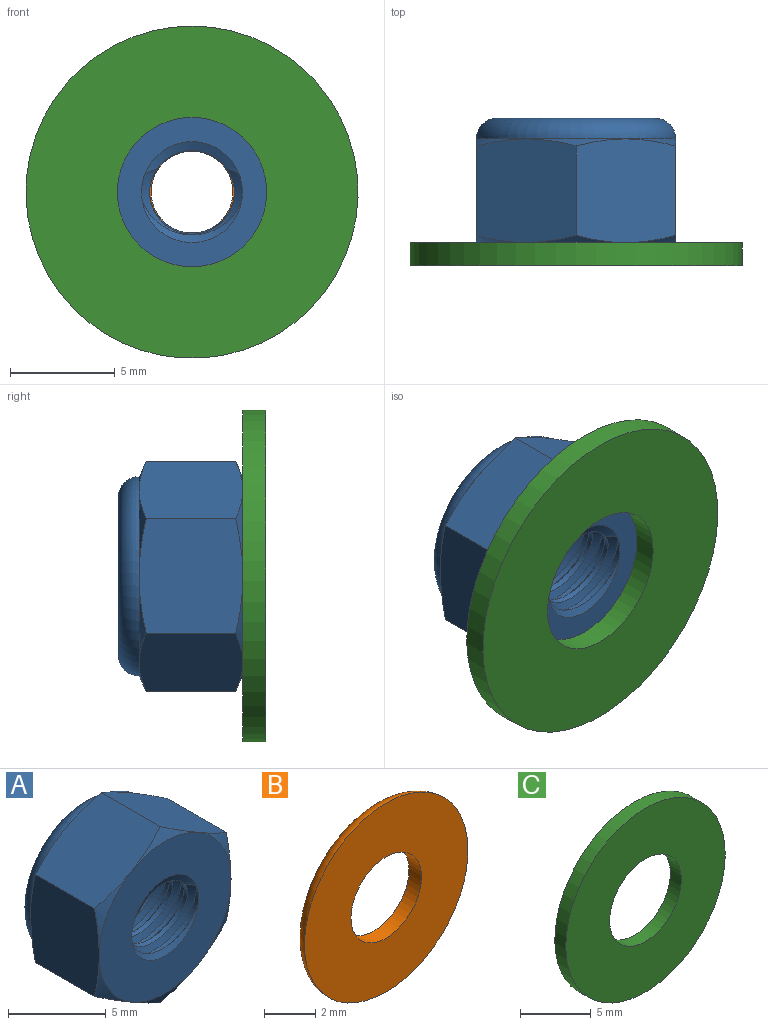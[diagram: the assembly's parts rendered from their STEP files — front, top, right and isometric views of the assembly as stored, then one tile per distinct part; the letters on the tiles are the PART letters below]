
ASSEMBLY  parts=3 mates=2
PART A: 50 faces, bbox 11.4x6.6x11.4 mm
  f0: torus R=3.77mm, axis (0,-1,0), area 35.7mm2, adj f48,f49
  f1: cylinder r=2.86mm len=5.72mm, axis (0,-1,0), area 2.7mm2, adj f26,f49
  f2: torus R=3.77mm, axis (0,-1,0), area 43.1mm2, adj f3,f26,f37,f38,f39,f40,f41
  f3: cone r=4.76mm half-angle=65deg, axis (0,-1,0), area 2.1mm2, adj f2,f46,f47
  f4: cone r=5.5mm half-angle=65deg, axis (0,1,0), area 2.1mm2, adj f27,f43,f44
  f5: cone r=2.6mm half-angle=60deg, axis (0,0.98,0.21), area 7.4mm2, adj f20,f23
  f6: cone r=2.03mm half-angle=60deg, axis (0,-0.98,-0.21), area 7.4mm2, adj f7,f20
  f7: cylinder r=2.03mm len=4.06mm, axis (0,0.98,0.21), area 3.4mm2, adj f6,f8
  f8: cone r=2.6mm half-angle=60deg, axis (0,0.98,0.21), area 7.4mm2, adj f7,f19
  f9: cone r=2.03mm half-angle=60deg, axis (0,-0.98,-0.21), area 7.4mm2, adj f10,f19
  f10: cylinder r=2.03mm len=4.06mm, axis (0,0.98,0.21), area 3.4mm2, adj f9,f11
  f11: cone r=2.6mm half-angle=60deg, axis (0,0.98,0.21), area 7.4mm2, adj f10,f18
  f12: cone r=2.03mm half-angle=60deg, axis (0,-0.98,-0.21), area 7.4mm2, adj f13,f18
  f13: cylinder r=2.03mm len=4.06mm, axis (0,0.98,0.21), area 3.4mm2, adj f12,f14
  f14: cone r=2.6mm half-angle=60deg, axis (0,0.98,0.21), area 7.4mm2, adj f13,f17
  f15: cylinder r=2.03mm len=4.06mm, axis (0,0.98,0.21), area 2.1mm2, adj f16,f31,f48
  f16: cone r=2.6mm half-angle=60deg, axis (0,0.98,0.21), area 2.6mm2, adj f15,f30,f48
  f17: cylinder r=2.41mm len=4.83mm, axis (0,-1,0), area 4.3mm2, adj f14,f31,f48
  f18: cylinder r=2.41mm len=4.83mm, axis (0,-1,0), area 4.4mm2, adj f11,f12
  f19: cylinder r=2.41mm len=4.83mm, axis (0,-1,0), area 4.4mm2, adj f8,f9
  f20: cylinder r=2.41mm len=4.83mm, axis (0,-1,0), area 4.4mm2, adj f5,f6
  f21: cylinder r=2.41mm len=4.83mm, axis (0,-1,0), area 1.9mm2, adj f22,f27,f29
  f22: cone r=2.03mm half-angle=60deg, axis (0,-0.98,-0.21), area 4.3mm2, adj f21,f23,f25
  f23: cylinder r=2.03mm len=4.06mm, axis (0,0.98,0.21), area 2.9mm2, adj f5,f22,f25
  f24: cone r=2.41mm half-angle=65deg, axis (0,-1,0), area 1.3mm2, adj f27,f29
  f25: cone r=2.41mm half-angle=65deg, axis (0,-1,0), area 2.2mm2, adj f22,f23,f27
  f26: plane 7.54x7.54mm, normal (0,1,0), area 18.9mm2, adj f1,f2
  f27: plane 9.53x9.53mm, normal (0,-1,0), area 53mm2, adj f4,f21,f24,f25,f32,f33,f34,f35
  f28: cone r=2.03mm half-angle=60deg, axis (0,-0.98,-0.21), area 0mm2, adj f30,f48
  f29: cone r=2.6mm half-angle=60deg, axis (0,0.98,0.21), area 1.6mm2, adj f21,f24
  f30: cylinder r=2.41mm len=4.45mm, axis (0,-1,0), area 0.9mm2, adj f16,f28,f48
  f31: cone r=2.03mm half-angle=60deg, axis (0,-0.98,-0.21), area 6.1mm2, adj f15,f17,f48
  f32: cone r=5.5mm half-angle=65deg, axis (0,1,0), area 2.1mm2, adj f27,f46,f47
  f33: cone r=5.5mm half-angle=65deg, axis (0,1,0), area 2.1mm2, adj f27,f42,f47
  f34: cone r=5.5mm half-angle=65deg, axis (0,1,0), area 2.1mm2, adj f27,f42,f43
  f35: cone r=5.5mm half-angle=65deg, axis (0,1,0), area 2.1mm2, adj f27,f44,f45
  f36: cone r=5.5mm half-angle=65deg, axis (0,1,0), area 2.1mm2, adj f27,f45,f46
  f37: cone r=4.76mm half-angle=65deg, axis (0,-1,0), area 2.1mm2, adj f2,f44,f45
  f38: cone r=4.76mm half-angle=65deg, axis (0,-1,0), area 2.1mm2, adj f2,f45,f46
  f39: cone r=4.76mm half-angle=65deg, axis (0,-1,0), area 2.1mm2, adj f2,f43,f44
  f40: cone r=4.76mm half-angle=65deg, axis (0,-1,0), area 2.1mm2, adj f2,f42,f47
  f41: cone r=4.76mm half-angle=65deg, axis (0,-1,0), area 2.1mm2, adj f2,f42,f43
  f42: plane 5.93x5.39mm, normal (1,0,0), area 26mm2, adj f33,f34,f40,f41,f43,f47
  f43: plane 5.39x5.19mm, normal (0.5,0,0.87), area 26mm2, adj f4,f34,f39,f41,f42,f44
  f44: plane 5.39x5.19mm, normal (-0.5,0,0.87), area 26mm2, adj f4,f35,f37,f39,f43,f45
  f45: plane 5.93x5.39mm, normal (-1,0,0), area 26mm2, adj f35,f36,f37,f38,f44,f46
  f46: plane 5.39x5.19mm, normal (-0.5,0,-0.87), area 26mm2, adj f3,f32,f36,f38,f45,f47
  f47: plane 5.39x5.19mm, normal (0.5,0,-0.87), area 26mm2, adj f3,f32,f33,f40,f42,f46
  f48: plane 9.38x9.38mm, normal (0,1,0), area 50.6mm2, adj f0,f15,f16,f17,f28,f30,f31
  f49: plane 7.54x7.54mm, normal (0,-1,0), area 18.9mm2, adj f0,f1
PART B: 4 faces, bbox 9.8x0.8x9.8 mm
  f0: torus R=3.77mm, axis (0,-1,0), area 29.9mm2, adj f2,f3
  f1: cylinder r=1.95mm len=3.91mm, axis (0,-1,0), area 8.4mm2, adj f2,f3
  f2: plane 9.06x9.06mm, normal (0,-1,0), area 52.5mm2, adj f0,f1
  f3: plane 7.54x7.54mm, normal (0,1,0), area 32.7mm2, adj f0,f1
PART C: 4 faces, bbox 15.9x1.1x15.9 mm
  f0: cylinder r=3.57mm len=7.14mm, axis (0,1,0), area 24.5mm2, adj f2,f3
  f1: cylinder r=7.94mm len=15.88mm, axis (0,-1,0), area 54.5mm2, adj f2,f3
  f2: plane 15.88x15.88mm, normal (0,1,0), area 157.9mm2, adj f0,f1
  f3: plane 15.88x15.88mm, normal (0,-1,0), area 157.9mm2, adj f0,f1
PLACE A t=(-2.21,-3.12,1.7)mm fixed
PLACE B t=(-2.21,-3.19,1.7)mm
PLACE C t=(-2.21,-4.21,1.7)mm
MATE fastened C.f0 <-> A.f2  axis (0,1,0) through (-2.21,-3.12,1.7)mm
MATE fastened B.f1 <-> A.f1  axis (0,-1,0) through (-2.21,1.84,1.7)mm
